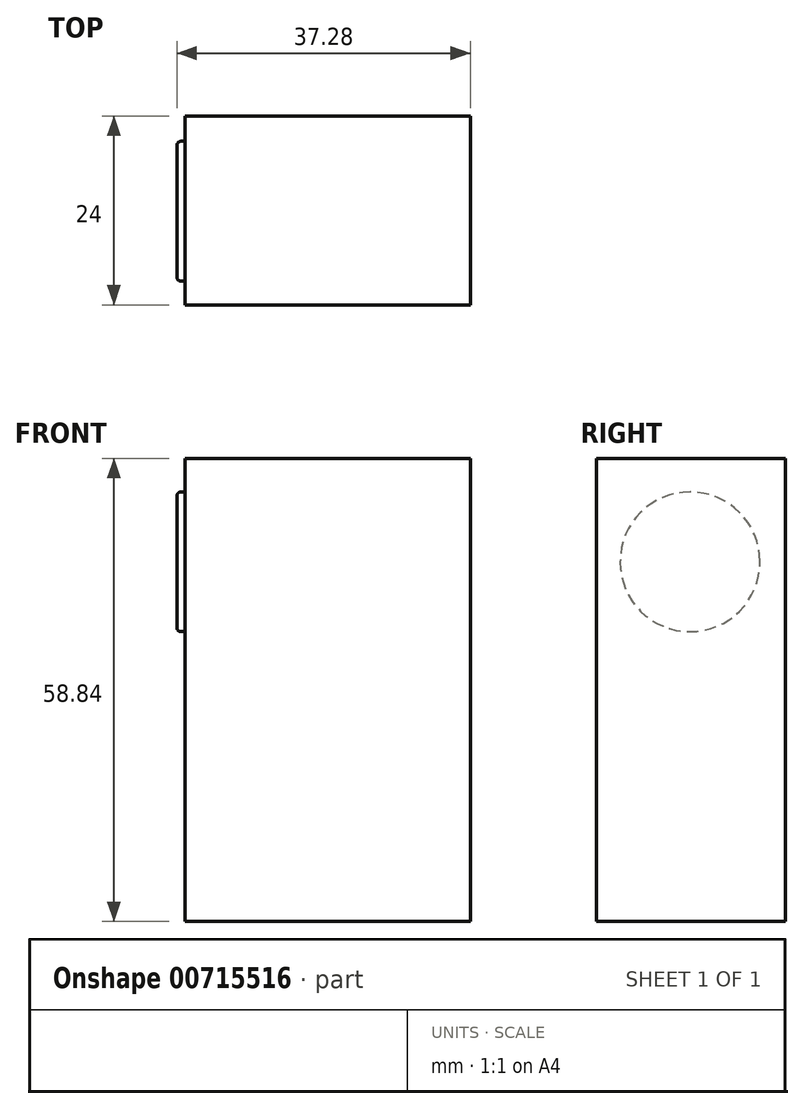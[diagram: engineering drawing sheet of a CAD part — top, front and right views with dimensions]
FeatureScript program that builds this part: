
annotation { "Feature Type Name" : "Feature", "Feature Type Description" : "" }
export const myFeature = defineFeature(function(context is Context, id is Id, definition is map)
    precondition{}
    {
        {
            var Q0;
            Q0=qCreatedBy(makeId("Front.planeOp"),FACE);
            var sketch = newSketch(context, id + "F0", { "sketchPlane" : qUnion([Q0])});
            skArc(sketch, "E0", {"start": v(49.23, -35.52) * mm, "mid": v(43.45, -42.4) * mm, "end": v(49.25, -49.27) * mm});
            skArc(sketch, "E1", {"start": v(49.23, -21.1) * mm, "mid": v(43.57, -28.32) * mm, "end": v(49.23, -35.52) * mm});
            skArc(sketch, "E2", {"start": v(49.23, -6.42) * mm, "mid": v(43.2, -13.77) * mm, "end": v(49.23, -21.1) * mm});
            skArc(sketch, "E3", {"start": v(49.23, 9.4) * mm, "mid": v(43.01, 1.49) * mm, "end": v(49.23, -6.42) * mm});
            skSolve(sketch);
        }
        {
            var Q0;
            Q0=qCreatedBy(makeId("Front.planeOp"),FACE);
            var sketch = newSketch(context, id + "F1", { "sketchPlane" : qUnion([Q0])});
            skLineSegment(sketch, "E4", {"start": v(49.17, 9.54) * mm, "end": v(23.77, 9.54) * mm});
            skLineSegment(sketch, "E5", {"start": v(23.77, 9.54) * mm, "end": v(23.77, -49.3) * mm});
            skLineSegment(sketch, "E6", {"start": v(23.77, -49.3) * mm, "end": v(49, -49.3) * mm});
            skSolve(sketch);
        }
        {
            var Q0;
            Q0 = qSketchRegion(id + "F1", true);
            var Q1;
            Q1 = qBodyType(qCreatedBy(id + "F0" ,EDGE), BodyType.WIRE);
            var Q2;
            Q2=sQuery(id+"F1.wireOp",EDGE,"E4");
            var Q3;
            Q3=sQuery(id+"F1.wireOp",EDGE,"E5");
            var Q4;
            Q4=sQuery(id+"F1.wireOp",EDGE,"E6");
            extrude(context, id + "F2", {"entities" : qUnion([Q0]), "bodyType" : ToolBodyType.SURFACE, "surfaceEntities" : qUnion([Q1, Q2, Q3, Q4]), "depth" : 24 * mm, "offsetDistance" : 25 * mm});
        }
        {
            var Q0;
            Q0=makeQuery(id+"F2.opExtrude","SWEPT_FACE",FACE,{"disambiguationData":[OSD([sQuery(id+"F1.wireOp",EDGE,"E5")])]});
            extrude(context, id + "F3", {"entities" : qUnion([Q0]), "depth" : 16.77 * mm, "offsetDistance" : 25 * mm});
        }
        {
            var Q0;
            Q0=makeQuery(id+"F2.opExtrude","SWEPT_FACE",FACE,{"disambiguationData":[OSD([sQuery(id+"F1.wireOp",EDGE,"E5")])]});
            extrude(context, id + "F4", {"entities" : qUnion([Q0]), "operationType" : NewBodyOperationType.ADD, "oppositeDirection" : true, "depth" : 19.5 * mm, "offsetDistance" : 25 * mm});
        }
        {
            var Q0;
            Q0=makeQuery(id+"F3.opExtrude","CAP_FACE",FACE,{"disambiguationData":[OSD([sQuery(id+"F1.wireOp",EDGE,"E5")])],"isStart":false});
            extrude(context, id + "F5", {"entities" : qUnion([Q0]), "operationType" : NewBodyOperationType.ADD, "oppositeDirection" : true, "depth" : 25 * mm, "offsetDistance" : 25 * mm});
        }
        {
            var Q0;
            Q0=makeQuery(id+"F3.opExtrude","CAP_FACE",FACE,{"disambiguationData":[OSD([sQuery(id+"F1.wireOp",EDGE,"E5")])],"isStart":false});
            var sketch = newSketch(context, id + "F6", { "sketchPlane" : qUnion([Q0])});
            skCircle(sketch, "E7", {"center": v(12.1, -3.6) * mm, "radius": 8.88 * mm});
            skSolve(sketch);
        }
        {
            var Q0;
            Q0 = qSketchRegion(id + "F6", true);
            extrude(context, id + "F7", {"entities" : qUnion([Q0]), "operationType" : NewBodyOperationType.ADD, "depth" : 1 * mm, "offsetDistance" : 25 * mm});
        }
        {
            var Q0;
            Q0=makeQuery(id+"F7.opExtrude","CAP_EDGE",EDGE,{"disambiguationData":[OSD([sQuery(id+"F6.wireOp",EDGE,"E7")])],"isStart":false});
            fillet(context, id + "F8", {"entities" : qUnion([Q0]), "radius" : 0.5 * mm, "tangentPropagation" : true, "allowEdgeOverflow" : false});
        }
    });
